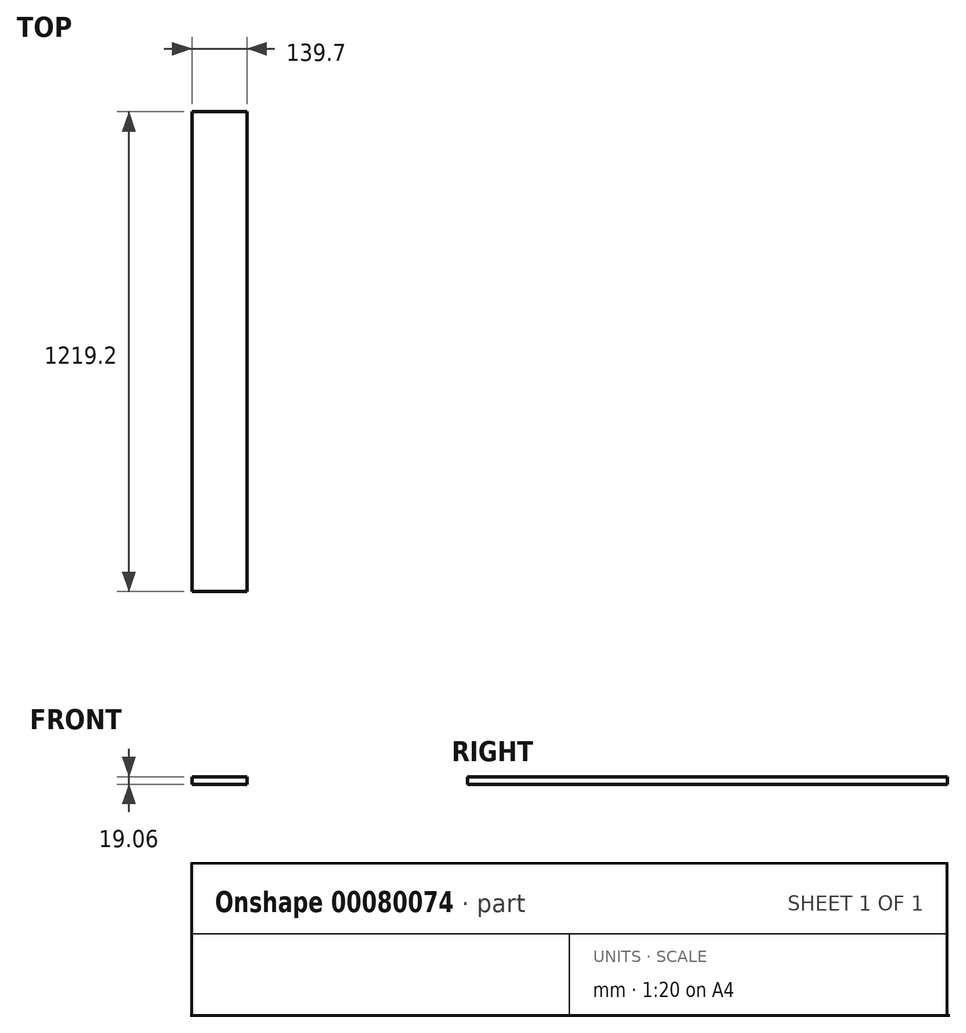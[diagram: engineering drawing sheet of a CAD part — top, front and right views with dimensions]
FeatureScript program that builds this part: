
annotation { "Feature Type Name" : "Feature", "Feature Type Description" : "" }
export const myFeature = defineFeature(function(context is Context, id is Id, definition is map)
    precondition{}
    {
        {
            var Q0;
            Q0=qCreatedBy(makeId("Front.planeOp"),FACE);
            var sketch = newSketch(context, id + "F0", { "sketchPlane" : qUnion([Q0])});
            skLineSegment(sketch, "E0.bottom", {"start": v(-69.85, 9.53) * mm, "end": v(69.85, 9.53) * mm});
            skLineSegment(sketch, "E0.top", {"start": v(-69.85, -9.52) * mm, "end": v(69.85, -9.52) * mm});
            skLineSegment(sketch, "E0.left", {"start": v(-69.85, 9.53) * mm, "end": v(-69.85, -9.52) * mm});
            skLineSegment(sketch, "E0.right", {"start": v(69.85, 9.53) * mm, "end": v(69.85, -9.52) * mm});
            skPoint(sketch, "E0.middle", {"position": v(0, 0) * mm});
            skSolve(sketch);
        }
        {
            var Q0;
            Q0=qSketchRegion(id+"F0",true);
            extrude(context, id + "F1", {"entities" : qUnion([Q0]), "endBound" : BoundingType.SYMMETRIC, "depth" : 1219.2 * mm});
        }
    });
